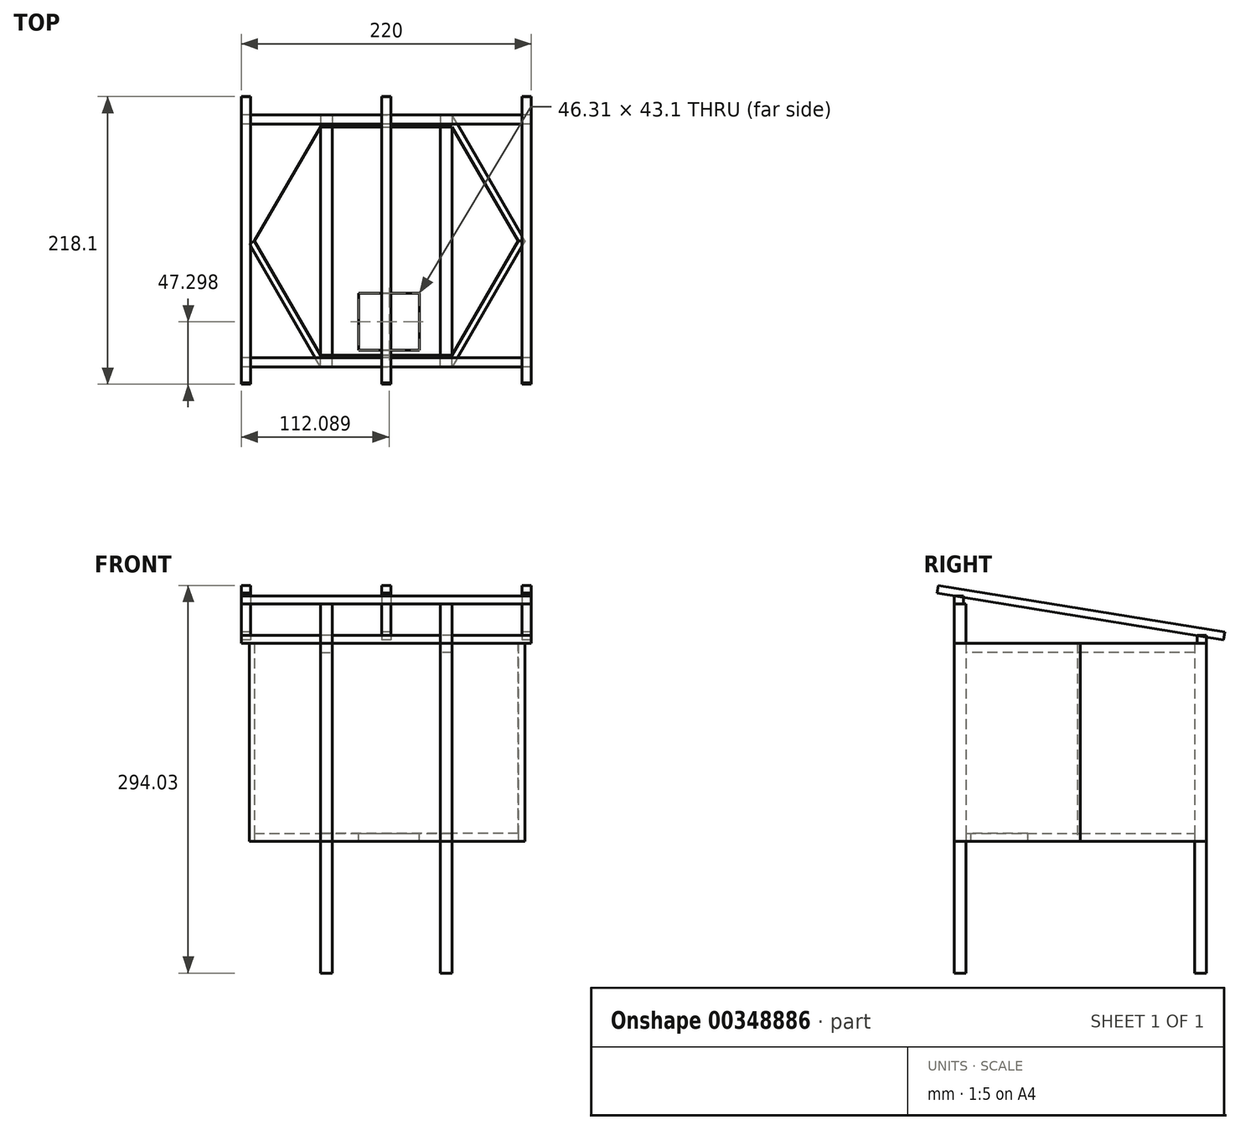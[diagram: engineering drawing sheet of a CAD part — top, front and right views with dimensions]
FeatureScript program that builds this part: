
annotation { "Feature Type Name" : "Feature", "Feature Type Description" : "" }
export const myFeature = defineFeature(function(context is Context, id is Id, definition is map)
    precondition{}
    {
        {
            var Q0;
            Q0=qCreatedBy(makeId("Top.planeOp"),FACE);
            var sketch = newSketch(context, id + "F0", { "sketchPlane" : qUnion([Q0])});
            skCircle(sketch, "E0.cCircle", {"center": v(0, 0) * mm, "radius": 86.6 * mm, "construction": true});
            skLineSegment(sketch, "E0.0", {"start": v(50, 86.6) * mm, "end": v(100, 0) * mm});
            skLineSegment(sketch, "E0.1", {"start": v(100, 0) * mm, "end": v(50, -86.6) * mm});
            skLineSegment(sketch, "E0.2", {"start": v(50, -86.6) * mm, "end": v(-50, -86.6) * mm});
            skLineSegment(sketch, "E0.3", {"start": v(-50, -86.6) * mm, "end": v(-100, 0) * mm});
            skLineSegment(sketch, "E0.4", {"start": v(-100, 0) * mm, "end": v(-50, 86.6) * mm});
            skLineSegment(sketch, "E0.5", {"start": v(-50, 86.6) * mm, "end": v(50, 86.6) * mm});
            skPoint(sketch, "E0.0.midPoint", {"position": v(75, 43.3) * mm});
            skLineSegment(sketch, "E1", {"start": v(-146.24, 86.6) * mm, "end": v(86.54, 86.6) * mm, "construction": true});
            skLineSegment(sketch, "E2", {"start": v(-88.7, 0) * mm, "end": v(0, 0) * mm, "construction": true});
            skPoint(sketch, "E2.endSnap0", {"position": v(0, -86.6) * mm});
            skLineSegment(sketch, "E3", {"start": v(0, 102.14) * mm, "end": v(0, -90.63) * mm, "construction": true});
            skPoint(sketch, "E3.startSnap0", {"position": v(0, 86.6) * mm});
            skSolve(sketch);
        }
        {
            var Q0;
            Q0 = qSketchRegion(id + "F0", true);
            extrude(context, id + "F1", {"entities" : qUnion([Q0]), "depth" : 6 * mm});
        }
        {
            var Q0;
            Q0=qCreatedBy(makeId("Top.planeOp"),FACE);
            var sketch = newSketch(context, id + "F2", { "sketchPlane" : qUnion([Q0])});
            skLineSegment(sketch, "E4.bottom", {"start": v(-50, 95.6) * mm, "end": v(-41, 95.6) * mm});
            skLineSegment(sketch, "E4.top", {"start": v(-50, 86.6) * mm, "end": v(-41, 86.6) * mm});
            skLineSegment(sketch, "E4.left", {"start": v(-50, 95.6) * mm, "end": v(-50, 86.6) * mm});
            skLineSegment(sketch, "E4.right", {"start": v(-41, 95.6) * mm, "end": v(-41, 86.6) * mm});
            skLineSegment(sketch, "E5", {"start": v(-41, -733.2) * mm, "end": v(-45.5, -538.98) * mm, "construction": true});
            skPoint(sketch, "E5.startSnap0", {"position": v(-41, 91.1) * mm});
            skPoint(sketch, "E5.endSnap0", {"position": v(-45.5, 95.6) * mm});
            skLineSegment(sketch, "E6", {"start": v(50, 110.57) * mm, "end": v(50, -106.48) * mm, "construction": true});
            skLineSegment(sketch, "E7", {"start": v(0, 118.71) * mm, "end": v(0, -106.48) * mm, "construction": true});
            skLineSegment(sketch, "E8", {"start": v(-50, 122.55) * mm, "end": v(-50, -106.48) * mm, "construction": true});
            skPoint(sketch, "E9.MirrorP", {"position": v(45.5, 95.6) * mm});
            skPoint(sketch, "E10.MirrorP", {"position": v(41, 91.1) * mm});
            skLineSegment(sketch, "E11.MirrorCS", {"start": v(50, 95.6) * mm, "end": v(41, 95.6) * mm});
            skLineSegment(sketch, "E12.MirrorCS", {"start": v(50, 86.6) * mm, "end": v(41, 86.6) * mm});
            skLineSegment(sketch, "E13.MirrorCS", {"start": v(50, 95.6) * mm, "end": v(50, 86.6) * mm});
            skLineSegment(sketch, "E14.MirrorCS", {"start": v(41, 95.6) * mm, "end": v(41, 86.6) * mm});
            skLineSegment(sketch, "E15", {"start": v(-110.42, 0) * mm, "end": v(140.1, 0) * mm, "construction": true});
            skLineSegment(sketch, "E16.MirrorCS", {"start": v(-41, -95.6) * mm, "end": v(-41, -86.6) * mm});
            skLineSegment(sketch, "E17.MirrorCS", {"start": v(50, -95.6) * mm, "end": v(41, -95.6) * mm});
            skLineSegment(sketch, "E18.MirrorCS", {"start": v(50, -86.6) * mm, "end": v(41, -86.6) * mm});
            skLineSegment(sketch, "E19.MirrorCS", {"start": v(50, -95.6) * mm, "end": v(50, -86.6) * mm});
            skLineSegment(sketch, "E20.MirrorCS", {"start": v(41, -95.6) * mm, "end": v(41, -86.6) * mm});
            skLineSegment(sketch, "E21.MirrorCS", {"start": v(-50, -86.6) * mm, "end": v(-41, -86.6) * mm});
            skLineSegment(sketch, "E22.MirrorCS", {"start": v(-50, -95.6) * mm, "end": v(-50, -86.6) * mm});
            skLineSegment(sketch, "E23.MirrorCS", {"start": v(-50, -95.6) * mm, "end": v(-41, -95.6) * mm});
            skPoint(sketch, "E24.MirrorP", {"position": v(-45.5, -95.6) * mm});
            skPoint(sketch, "E25.MirrorP", {"position": v(45.5, -95.6) * mm});
            skPoint(sketch, "E26.MirrorP", {"position": v(41, -91.1) * mm});
            skPoint(sketch, "E27.MirrorP", {"position": v(-41, -91.1) * mm});
            skSolve(sketch);
        }
        {
            var Q0;
            Q0 = qSketchRegion(id + "F2", true);
            extrude(context, id + "F3", {"entities" : qUnion([Q0]), "depth" : 150 * mm, "offsetDistance" : 25 * mm});
        }
        {
            var Q0;
            Q0=qCreatedBy(makeId("Top.planeOp"),FACE);
            cPlane(context, id + "F4", {"entities" : qUnion([Q0]), "cplaneType" : CPlaneType.OFFSET, "offset" : 150 * mm, "width" : 150 * mm, "height" : 150 * mm});
        }
        {
            var Q0;
            Q0=qCreatedBy(id+"F4.planeOp",FACE);
            var sketch = newSketch(context, id + "F5", { "sketchPlane" : qUnion([Q0])});
            skLineSegment(sketch, "E28.bottom", {"start": v(-41, 95.6) * mm, "end": v(41, 95.6) * mm});
            skLineSegment(sketch, "E28.top", {"start": v(-41, 86.6) * mm, "end": v(41, 86.6) * mm});
            skLineSegment(sketch, "E28.left", {"start": v(-41, 95.6) * mm, "end": v(-41, 86.6) * mm});
            skLineSegment(sketch, "E28.right", {"start": v(41, 95.6) * mm, "end": v(41, 86.6) * mm});
            skSolve(sketch);
        }
        {
            var Q0;
            Q0 = qSketchRegion(id + "F5", true);
            extrude(context, id + "F6", {"entities" : qUnion([Q0]), "oppositeDirection" : true, "depth" : 150 * mm});
        }
        {
            var Q0;
            Q0=makeQuery(id+"F6.opExtrude","SWEPT_BODY",BODY,{"disambiguationData":[OSD([sQuery(id+"F5.wireOp",EDGE,"E28.bottom"),sQuery(id+"F5.wireOp",EDGE,"E28.top"),sQuery(id+"F5.wireOp",EDGE,"E28.left"),sQuery(id+"F5.wireOp",EDGE,"E28.right")])]});
            var Q1;
            Q1=qCreatedBy(makeId("Front.planeOp"),FACE);
            mirror(context, id + "F7", {"entities" : qUnion([Q0]), "mirrorPlane" : qUnion([Q1])});
        }
        {
            var Q0;
            Q0 = qSketchRegion(id + "F2", true);
            var Q1;
            Q1 = qConstructionFilter(qBodyType(qCreatedBy(id + "F2" ,EDGE), BodyType.WIRE), ConstructionObject.NO);
            extrude(context, id + "F8", {"entities" : qUnion([Q0]), "surfaceEntities" : qUnion([Q1]), "oppositeDirection" : true, "depth" : 100 * mm});
        }
        {
            var Q0;
            Q0=qCreatedBy(id+"F4.planeOp",FACE);
            var sketch = newSketch(context, id + "F9", { "sketchPlane" : qUnion([Q0])});
            skLineSegment(sketch, "E29", {"start": v(50, 86.6) * mm, "end": v(100, 0) * mm});
            skLineSegment(sketch, "E30", {"start": v(100, 0) * mm, "end": v(105.2, 0) * mm});
            skLineSegment(sketch, "E31", {"start": v(105.2, 0) * mm, "end": v(50, 95.6) * mm});
            skLineSegment(sketch, "E32", {"start": v(50, 95.6) * mm, "end": v(50, 86.6) * mm});
            skLineSegment(sketch, "E33", {"start": v(0, 117.97) * mm, "end": v(0, 29.71) * mm, "construction": true});
            skSolve(sketch);
        }
        {
            var Q0;
            Q0 = qSketchRegion(id + "F9", true);
            extrude(context, id + "F10", {"entities" : qUnion([Q0]), "operationType" : NewBodyOperationType.ADD, "oppositeDirection" : true, "depth" : 150 * mm});
        }
        {
            var Q0;
            Q0=qCreatedBy(makeId("Front.planeOp"),FACE);
            var sketch = newSketch(context, id + "F11", { "sketchPlane" : qUnion([Q0])});
            skLineSegment(sketch, "E34", {"start": v(0, 297.87) * mm, "end": v(0, -100.74) * mm, "construction": true});
            skCircle(sketch, "E35", {"center": v(0, 226.82) * mm, "radius": 12.33 * mm, "construction": true});
            skSolve(sketch);
        }
        {
            var Q0;
            Q0=makeQuery(id+"F1.opExtrude","CAP_FACE",FACE,{"disambiguationData":[OSD([sQuery(id+"F0.wireOp",EDGE,"E0.0"),sQuery(id+"F0.wireOp",EDGE,"E0.1"),sQuery(id+"F0.wireOp",EDGE,"E0.2"),sQuery(id+"F0.wireOp",EDGE,"E0.3"),sQuery(id+"F0.wireOp",EDGE,"E0.4"),sQuery(id+"F0.wireOp",EDGE,"E0.5")])],"isStart":false});
            var sketch = newSketch(context, id + "F12", { "sketchPlane" : qUnion([Q0])});
            skLineSegment(sketch, "E36.bottom", {"start": v(-21.07, -39.72) * mm, "end": v(25.24, -39.72) * mm});
            skLineSegment(sketch, "E36.top", {"start": v(-21.07, -82.82) * mm, "end": v(25.24, -82.82) * mm});
            skLineSegment(sketch, "E36.left", {"start": v(-21.07, -39.72) * mm, "end": v(-21.07, -82.82) * mm});
            skLineSegment(sketch, "E36.right", {"start": v(25.24, -39.72) * mm, "end": v(25.24, -82.82) * mm});
            skSolve(sketch);
        }
        {
            var Q0;
            Q0=makeQuery(id+"F12.imprint","IMPRINT",FACE,{"disambiguationData":[TD([[makeQuery(id+"F12.imprint","IMPRINT",EDGE,{"derivedFrom":sQuery(id+"F12.wireOp",EDGE,"E36.bottom")}),-1.0]])]});
            extrude(context, id + "F13", {"entities" : qUnion([Q0]), "operationType" : NewBodyOperationType.REMOVE, "endBound" : BoundingType.UP_TO_NEXT, "oppositeDirection" : true, "depth" : 25 * mm});
        }
        {
            var Q0;
            Q0=qCreatedBy(makeId("Top.planeOp"),FACE);
            var sketch = newSketch(context, id + "F14", { "sketchPlane" : qUnion([Q0])});
            skLineSegment(sketch, "E37", {"start": v(100, 0) * mm, "end": v(105.2, 0) * mm});
            skLineSegment(sketch, "E38", {"start": v(105.2, 0) * mm, "end": v(50, -95.6) * mm});
            skLineSegment(sketch, "E39", {"start": v(50, -95.6) * mm, "end": v(50, -86.6) * mm});
            skLineSegment(sketch, "E40", {"start": v(50, -86.6) * mm, "end": v(100, 0) * mm});
            skSolve(sketch);
        }
        {
            var Q0;
            Q0=qCreatedBy(makeId("Top.planeOp"),FACE);
            var sketch = newSketch(context, id + "F15", { "sketchPlane" : qUnion([Q0])});
            skLineSegment(sketch, "E41", {"start": v(-103.82, -2.2) * mm, "end": v(-100, 0) * mm});
            skLineSegment(sketch, "E42", {"start": v(-100, 0) * mm, "end": v(-50, -86.6) * mm});
            skLineSegment(sketch, "E43", {"start": v(-50, -86.6) * mm, "end": v(-50, -95.6) * mm});
            skLineSegment(sketch, "E44", {"start": v(-50, -95.6) * mm, "end": v(-103.82, -2.2) * mm});
            skSolve(sketch);
        }
        {
            var Q0;
            Q0 = qSketchRegion(id + "F14", true);
            extrude(context, id + "F16", {"entities" : qUnion([Q0]), "depth" : 150 * mm});
        }
        {
            var Q0;
            Q0 = qSketchRegion(id + "F15", true);
            extrude(context, id + "F17", {"entities" : qUnion([Q0]), "depth" : 150 * mm});
        }
        {
            var Q0;
            Q0=makeQuery(id+"F3.opExtrude","SWEPT_FACE",FACE,{"disambiguationData":[OSD([sQuery(id+"F2.wireOp",EDGE,"E21.MirrorCS")])]});
            var sketch = newSketch(context, id + "F18", { "sketchPlane" : qUnion([Q0])});
            skLineSegment(sketch, "E45.bottom", {"start": v(50, 150) * mm, "end": v(41, 150) * mm});
            skLineSegment(sketch, "E45.top", {"start": v(50, 143) * mm, "end": v(41, 143) * mm});
            skLineSegment(sketch, "E45.left", {"start": v(50, 150) * mm, "end": v(50, 143) * mm});
            skLineSegment(sketch, "E45.right", {"start": v(41, 150) * mm, "end": v(41, 143) * mm});
            skLineSegment(sketch, "E46.bottom", {"start": v(-41, 150) * mm, "end": v(-50, 150) * mm});
            skLineSegment(sketch, "E46.top", {"start": v(-41, 143) * mm, "end": v(-50, 143) * mm});
            skLineSegment(sketch, "E46.left", {"start": v(-41, 150) * mm, "end": v(-41, 143) * mm});
            skLineSegment(sketch, "E46.right", {"start": v(-50, 150) * mm, "end": v(-50, 143) * mm});
            skSolve(sketch);
        }
        {
            var Q0;
            Q0 = qSketchRegion(id + "F18", true);
            extrude(context, id + "F19", {"entities" : qUnion([Q0]), "endBound" : BoundingType.UP_TO_NEXT, "depth" : 25 * mm, "offsetDistance" : 25 * mm});
        }
        {
            var Q0;
            Q0=makeQuery(id+"F6.opExtrude","CAP_FACE",FACE,{"disambiguationData":[OSD([sQuery(id+"F5.wireOp",EDGE,"E28.bottom"),sQuery(id+"F5.wireOp",EDGE,"E28.top"),sQuery(id+"F5.wireOp",EDGE,"E28.left"),sQuery(id+"F5.wireOp",EDGE,"E28.right")])],"isStart":true});
            var sketch = newSketch(context, id + "F20", { "sketchPlane" : qUnion([Q0])});
            skLineSegment(sketch, "E47.bottom", {"start": v(110, 88.6) * mm, "end": v(-110, 88.6) * mm});
            skLineSegment(sketch, "E47.top", {"start": v(110, 95.6) * mm, "end": v(-110, 95.6) * mm});
            skLineSegment(sketch, "E47.left", {"start": v(110, 88.6) * mm, "end": v(110, 95.6) * mm});
            skLineSegment(sketch, "E47.right", {"start": v(-110, 88.6) * mm, "end": v(-110, 95.6) * mm});
            skSolve(sketch);
        }
        {
            var Q0;
            Q0 = qSketchRegion(id + "F20", true);
            extrude(context, id + "F21", {"entities" : qUnion([Q0]), "depth" : 6 * mm, "offsetDistance" : 25 * mm});
        }
        {
            var Q0;
            Q0=makeQuery(id+"F7.opPattern","COPY",FACE,{"derivedFrom":makeQuery(id+"F6.opExtrude","CAP_FACE",FACE,{"disambiguationData":[OSD([sQuery(id+"F5.wireOp",EDGE,"E28.bottom"),sQuery(id+"F5.wireOp",EDGE,"E28.top"),sQuery(id+"F5.wireOp",EDGE,"E28.left"),sQuery(id+"F5.wireOp",EDGE,"E28.right")])],"isStart":true}),"instanceName":"1"});
            var sketch = newSketch(context, id + "F22", { "sketchPlane" : qUnion([Q0])});
            skLineSegment(sketch, "E48.bottom", {"start": v(41, -95.6) * mm, "end": v(50, -95.6) * mm});
            skLineSegment(sketch, "E48.top", {"start": v(41, -86.6) * mm, "end": v(50, -86.6) * mm});
            skLineSegment(sketch, "E48.left", {"start": v(41, -95.6) * mm, "end": v(41, -86.6) * mm});
            skLineSegment(sketch, "E48.right", {"start": v(50, -95.6) * mm, "end": v(50, -86.6) * mm});
            skLineSegment(sketch, "E49.bottom", {"start": v(-50, -95.6) * mm, "end": v(-41, -95.6) * mm});
            skLineSegment(sketch, "E49.top", {"start": v(-50, -86.6) * mm, "end": v(-41, -86.6) * mm});
            skLineSegment(sketch, "E49.left", {"start": v(-50, -95.6) * mm, "end": v(-50, -86.6) * mm});
            skLineSegment(sketch, "E49.right", {"start": v(-41, -95.6) * mm, "end": v(-41, -86.6) * mm});
            skSolve(sketch);
        }
        {
            var Q0;
            Q0 = qSketchRegion(id + "F22", true);
            extrude(context, id + "F23", {"entities" : qUnion([Q0]), "depth" : 30 * mm, "offsetDistance" : 25 * mm});
        }
        {
            var Q0;
            Q0=makeQuery(id+"F23.opExtrude","CAP_FACE",FACE,{"disambiguationData":[OSD([sQuery(id+"F22.wireOp",EDGE,"E48.bottom"),sQuery(id+"F22.wireOp",EDGE,"E48.top"),sQuery(id+"F22.wireOp",EDGE,"E48.left"),sQuery(id+"F22.wireOp",EDGE,"E48.right")])],"isStart":false});
            var sketch = newSketch(context, id + "F24", { "sketchPlane" : qUnion([Q0])});
            skLineSegment(sketch, "E50.bottom", {"start": v(110, -95.6) * mm, "end": v(-110, -95.6) * mm});
            skLineSegment(sketch, "E50.top", {"start": v(110, -88.6) * mm, "end": v(-110, -88.6) * mm});
            skLineSegment(sketch, "E50.left", {"start": v(-110, -95.6) * mm, "end": v(-110, -88.6) * mm});
            skLineSegment(sketch, "E50.right", {"start": v(110, -95.6) * mm, "end": v(110, -88.6) * mm});
            skSolve(sketch);
        }
        {
            var Q0;
            Q0 = qSketchRegion(id + "F24", true);
            extrude(context, id + "F25", {"entities" : qUnion([Q0]), "depth" : 6 * mm, "offsetDistance" : 25 * mm});
        }
        {
            var Q0;
            Q0=makeQuery(id+"F21.opExtrude","CAP_VERTEX",VERTEX,{"disambiguationData":[OSD([sQuery(id+"F20.wireOp",EDGE,"E47.bottom"),sQuery(id+"F20.wireOp",EDGE,"E47.left")])],"isStart":false});
            var Q1;
            Q1=makeQuery(id+"F25.opExtrude","CAP_VERTEX",VERTEX,{"disambiguationData":[OSD([sQuery(id+"F24.wireOp",EDGE,"E50.bottom"),sQuery(id+"F24.wireOp",EDGE,"E50.right")])],"isStart":false});
            var Q2;
            Q2=makeQuery(id+"F25.opExtrude","CAP_VERTEX",VERTEX,{"disambiguationData":[OSD([sQuery(id+"F24.wireOp",EDGE,"E50.bottom"),sQuery(id+"F24.wireOp",EDGE,"E50.left")])],"isStart":false});
            cPlane(context, id + "F26", {"entities" : qUnion([Q0, Q1, Q2]), "cplaneType" : CPlaneType.THREE_POINT, "offset" : 25 * mm, "width" : 150 * mm, "height" : 150 * mm});
        }
        {
            var Q0;
            Q0=qCreatedBy(id+"F26.planeOp",FACE);
            var sketch = newSketch(context, id + "F27", { "sketchPlane" : qUnion([Q0])});
            skLineSegment(sketch, "E51.bottom", {"start": v(110, -137.4) * mm, "end": v(103, -137.4) * mm});
            skLineSegment(sketch, "E51.top", {"start": v(110, 82.6) * mm, "end": v(103, 82.6) * mm});
            skLineSegment(sketch, "E51.left", {"start": v(110, -137.4) * mm, "end": v(110, 82.6) * mm});
            skLineSegment(sketch, "E51.right", {"start": v(103, -137.4) * mm, "end": v(103, 82.6) * mm});
            skLineSegment(sketch, "E52.bottom", {"start": v(-250.42, -16.9) * mm, "end": v(-275.27, -16.9) * mm});
            skLineSegment(sketch, "E52.top", {"start": v(-250.42, 138.18) * mm, "end": v(-275.27, 138.18) * mm});
            skLineSegment(sketch, "E52.left", {"start": v(-250.42, -16.9) * mm, "end": v(-250.42, 138.18) * mm});
            skLineSegment(sketch, "E52.right", {"start": v(-275.27, -16.9) * mm, "end": v(-275.27, 138.18) * mm});
            skLineSegment(sketch, "E53.bottom", {"start": v(-716.04, -12.47) * mm, "end": v(-737.59, -12.47) * mm});
            skLineSegment(sketch, "E53.top", {"start": v(-716.04, 233.34) * mm, "end": v(-737.59, 233.34) * mm});
            skLineSegment(sketch, "E53.left", {"start": v(-716.04, -12.47) * mm, "end": v(-716.04, 233.34) * mm});
            skLineSegment(sketch, "E53.right", {"start": v(-737.59, -12.47) * mm, "end": v(-737.59, 233.34) * mm});
            skLineSegment(sketch, "E54.1.0.0", {"start": v(-3.5, -137.4) * mm, "end": v(-3.5, 82.6) * mm});
            skLineSegment(sketch, "E54.1.0.1", {"start": v(3.5, -137.4) * mm, "end": v(3.5, 82.6) * mm});
            skLineSegment(sketch, "E54.1.0.2", {"start": v(3.5, 82.6) * mm, "end": v(-3.5, 82.6) * mm});
            skLineSegment(sketch, "E54.1.0.3", {"start": v(3.5, -137.4) * mm, "end": v(-3.5, -137.4) * mm});
            skLineSegment(sketch, "E54.2.0.0", {"start": v(-110, -137.4) * mm, "end": v(-110, 82.6) * mm});
            skLineSegment(sketch, "E54.2.0.1", {"start": v(-103, -137.4) * mm, "end": v(-103, 82.6) * mm});
            skLineSegment(sketch, "E54.2.0.2", {"start": v(-103, 82.6) * mm, "end": v(-110, 82.6) * mm});
            skLineSegment(sketch, "E54.2.0.3", {"start": v(-103, -137.4) * mm, "end": v(-110, -137.4) * mm});
            skLineSegment(sketch, "E54.direction1", {"start": v(103, -137.4) * mm, "end": v(-3.5, -137.4) * mm, "construction": true});
            skSolve(sketch);
        }
        {
            var Q0;
            Q0=makeQuery(id+"F27.imprint","IMPRINT",FACE,{"disambiguationData":[TD([[makeQuery(id+"F27.imprint","IMPRINT",EDGE,{"derivedFrom":sQuery(id+"F27.wireOp",EDGE,"E54.2.0.0")}),-1.0]])]});
            var Q1;
            Q1=makeQuery(id+"F27.imprint","IMPRINT",FACE,{"disambiguationData":[TD([[makeQuery(id+"F27.imprint","IMPRINT",EDGE,{"derivedFrom":sQuery(id+"F27.wireOp",EDGE,"E54.1.0.0")}),-1.0]])]});
            var Q2;
            Q2=makeQuery(id+"F27.imprint","IMPRINT",FACE,{"disambiguationData":[TD([[makeQuery(id+"F27.imprint","IMPRINT",EDGE,{"derivedFrom":sQuery(id+"F27.wireOp",EDGE,"E51.bottom")}),-1.0]])]});
            extrude(context, id + "F28", {"entities" : qUnion([Q0, Q1, Q2]), "depth" : 6 * mm, "offsetDistance" : 25 * mm});
        }
    });
